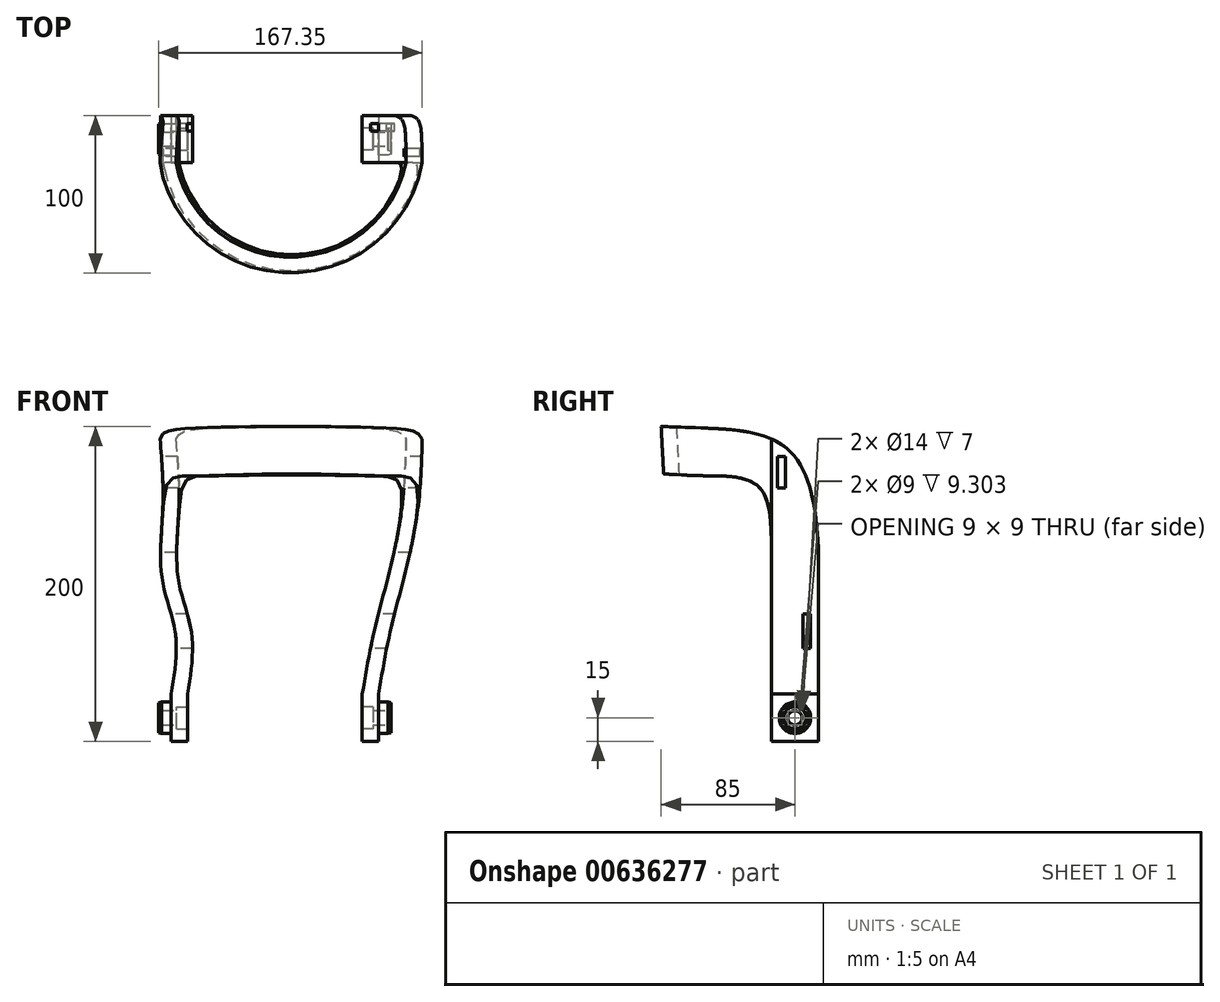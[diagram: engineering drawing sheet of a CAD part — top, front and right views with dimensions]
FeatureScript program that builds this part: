
annotation { "Feature Type Name" : "Feature", "Feature Type Description" : "" }
export const myFeature = defineFeature(function(context is Context, id is Id, definition is map)
    precondition{}
    {
        {
            var Q0;
            Q0=qCreatedBy(makeId("Top.planeOp"),FACE);
            var sketch = newSketch(context, id + "F0", { "sketchPlane" : qUnion([Q0])});
            skLineSegment(sketch, "E0", {"start": v(-55.5, 15) * mm, "end": v(-55.5, -15) * mm});
            skLineSegment(sketch, "E1", {"start": v(55.5, 15) * mm, "end": v(55.5, -15) * mm});
            skPoint(sketch, "E2", {"position": v(-55.5, 0) * mm});
            skPoint(sketch, "E3", {"position": v(55.5, 0) * mm});
            skLineSegment(sketch, "E4", {"start": v(-55.5, 15) * mm, "end": v(-65.81, 15) * mm});
            skLineSegment(sketch, "E5", {"start": v(-65.81, 15) * mm, "end": v(-65.81, -15) * mm});
            skLineSegment(sketch, "E6", {"start": v(55.5, 15) * mm, "end": v(65.81, 15) * mm});
            skLineSegment(sketch, "E7", {"start": v(65.81, 15) * mm, "end": v(65.81, -15) * mm});
            skLineSegment(sketch, "E8", {"start": v(-65.81, -15) * mm, "end": v(-55.5, -15) * mm});
            skLineSegment(sketch, "E9", {"start": v(55.5, -15) * mm, "end": v(65.81, -15) * mm});
            skSolve(sketch);
        }
        {
            var Q0;
            Q0=qCreatedBy(makeId("Top.planeOp"),FACE);
            cPlane(context, id + "F1", {"entities" : qUnion([Q0]), "cplaneType" : CPlaneType.OFFSET, "offset" : 30 * mm, "width" : 150 * mm, "height" : 150 * mm});
        }
        {
            var Q0;
            Q0=qCreatedBy(id+"F1.planeOp",FACE);
            var sketch = newSketch(context, id + "F2", { "sketchPlane" : qUnion([Q0])});
            skArc(sketch, "E10", {"start": v(-55.5, -15) * mm, "mid": v(0, -57.5) * mm, "end": v(55.5, -15) * mm});
            skArc(sketch, "E11", {"start": v(-65.81, -15) * mm, "mid": v(0, -67.5) * mm, "end": v(65.81, -15) * mm});
            skLineSegment(sketch, "E12", {"start": v(-55.5, 15) * mm, "end": v(-55.5, -15) * mm});
            skLineSegment(sketch, "E13", {"start": v(55.5, 15) * mm, "end": v(55.5, -15) * mm});
            skPoint(sketch, "E14", {"position": v(-55.5, 0) * mm});
            skPoint(sketch, "E15", {"position": v(55.5, 0) * mm});
            skLineSegment(sketch, "E16", {"start": v(-55.5, 15) * mm, "end": v(-65.81, 15) * mm});
            skLineSegment(sketch, "E17", {"start": v(-65.81, 15) * mm, "end": v(-65.81, -15) * mm});
            skLineSegment(sketch, "E18", {"start": v(55.5, 15) * mm, "end": v(65.81, 15) * mm});
            skLineSegment(sketch, "E19", {"start": v(65.81, 15) * mm, "end": v(65.81, -15) * mm});
            skSolve(sketch);
        }
        {
            var Q0;
            Q0=qCreatedBy(makeId("Top.planeOp"),FACE);
            cPlane(context, id + "F3", {"entities" : qUnion([Q0]), "cplaneType" : CPlaneType.OFFSET, "offset" : 70 * mm, "width" : 150 * mm, "height" : 150 * mm});
        }
        {
            var Q0;
            Q0=qCreatedBy(id+"F3.planeOp",FACE);
            var sketch = newSketch(context, id + "F4", { "sketchPlane" : qUnion([Q0])});
            skPoint(sketch, "E20", {"position": v(5, 0) * mm});
            skPoint(sketch, "E21.center.orphan", {"position": v(0, 0) * mm});
            skArc(sketch, "E22", {"start": v(-53.1, -15) * mm, "mid": v(5, -60) * mm, "end": v(63.1, -15) * mm});
            skArc(sketch, "E23", {"start": v(-63.37, -15) * mm, "mid": v(5, -70) * mm, "end": v(73.37, -15) * mm});
            skLineSegment(sketch, "E24", {"start": v(-53.1, 15) * mm, "end": v(-53.1, -15) * mm});
            skLineSegment(sketch, "E25", {"start": v(63.1, 15) * mm, "end": v(63.1, -15) * mm});
            skPoint(sketch, "E26", {"position": v(-53.1, 0) * mm});
            skLineSegment(sketch, "E27", {"start": v(-53.1, 15) * mm, "end": v(-63.37, 15) * mm});
            skLineSegment(sketch, "E28", {"start": v(-63.37, 15) * mm, "end": v(-63.37, -15) * mm});
            skLineSegment(sketch, "E29", {"start": v(63.1, 15) * mm, "end": v(73.37, 15) * mm});
            skLineSegment(sketch, "E30", {"start": v(73.37, 15) * mm, "end": v(73.37, -15) * mm});
            skSolve(sketch);
        }
        {
            var Q0;
            Q0=qCreatedBy(makeId("Top.planeOp"),FACE);
            cPlane(context, id + "F5", {"entities" : qUnion([Q0]), "cplaneType" : CPlaneType.OFFSET, "offset" : 100 * mm, "width" : 150 * mm, "height" : 150 * mm});
        }
        {
            var Q0;
            Q0=qCreatedBy(id+"F5.planeOp",FACE);
            var sketch = newSketch(context, id + "F6", { "sketchPlane" : qUnion([Q0])});
            skPoint(sketch, "E31", {"position": v(5, 0) * mm});
            skArc(sketch, "E32", {"start": v(-60.81, -15) * mm, "mid": v(5, -67.5) * mm, "end": v(70.81, -15) * mm});
            skArc(sketch, "E33", {"start": v(-71.03, -15) * mm, "mid": v(5, -77.5) * mm, "end": v(81.03, -15) * mm});
            skLineSegment(sketch, "E34", {"start": v(-60.81, 15) * mm, "end": v(-60.81, -15) * mm});
            skLineSegment(sketch, "E35", {"start": v(70.81, 15) * mm, "end": v(70.81, -15) * mm});
            skLineSegment(sketch, "E36", {"start": v(-60.81, 15) * mm, "end": v(-71.03, 15) * mm});
            skLineSegment(sketch, "E37", {"start": v(-71.03, 15) * mm, "end": v(-71.03, -15) * mm});
            skLineSegment(sketch, "E38", {"start": v(70.81, 15) * mm, "end": v(81.03, 15) * mm});
            skLineSegment(sketch, "E39", {"start": v(81.03, 15) * mm, "end": v(81.03, -15) * mm});
            skSolve(sketch);
        }
        {
            var Q0;
            Q0=qCreatedBy(makeId("Top.planeOp"),FACE);
            cPlane(context, id + "F7", {"entities" : qUnion([Q0]), "cplaneType" : CPlaneType.OFFSET, "offset" : 150 * mm, "width" : 150 * mm, "height" : 150 * mm});
        }
        {
            var Q0;
            Q0=qCreatedBy(id+"F7.planeOp",FACE);
            var sketch = newSketch(context, id + "F8", { "sketchPlane" : qUnion([Q0])});
            skPoint(sketch, "E40", {"position": v(10, 0) * mm});
            skArc(sketch, "E41", {"start": v(-60.93, -15) * mm, "mid": v(10, -72.5) * mm, "end": v(80.93, -15) * mm});
            skArc(sketch, "E42", {"start": v(-71.12, -15) * mm, "mid": v(10, -82.5) * mm, "end": v(91.12, -15) * mm});
            skLineSegment(sketch, "E43", {"start": v(-60.93, 15) * mm, "end": v(-60.93, -15) * mm});
            skLineSegment(sketch, "E44", {"start": v(80.93, -15) * mm, "end": v(80.93, 15) * mm});
            skPoint(sketch, "E45", {"position": v(-60.93, 0) * mm});
            skPoint(sketch, "E46", {"position": v(80.93, 0) * mm});
            skLineSegment(sketch, "E47", {"start": v(-60.93, 15) * mm, "end": v(-71.12, 15) * mm});
            skLineSegment(sketch, "E48", {"start": v(-71.12, 15) * mm, "end": v(-71.12, -15) * mm});
            skLineSegment(sketch, "E49", {"start": v(80.93, 15) * mm, "end": v(91.12, 15) * mm});
            skLineSegment(sketch, "E50", {"start": v(91.12, 15) * mm, "end": v(91.12, -15) * mm});
            skSolve(sketch);
        }
        {
            var Q0;
            Q0=qCreatedBy(makeId("Top.planeOp"),FACE);
            cPlane(context, id + "F9", {"entities" : qUnion([Q0]), "cplaneType" : CPlaneType.OFFSET, "offset" : 200 * mm, "width" : 150 * mm, "height" : 150 * mm});
        }
        {
            var Q0;
            Q0=qCreatedBy(id+"F9.planeOp",FACE);
            var sketch = newSketch(context, id + "F10", { "sketchPlane" : qUnion([Q0])});
            skPoint(sketch, "E51", {"position": v(10, 0) * mm});
            skArc(sketch, "E52", {"start": v(-63.48, -15) * mm, "mid": v(10, -75) * mm, "end": v(83.48, -15) * mm});
            skArc(sketch, "E53", {"start": v(-73.67, -15) * mm, "mid": v(10, -85) * mm, "end": v(93.67, -15) * mm});
            skLineSegment(sketch, "E54", {"start": v(-63.48, 15) * mm, "end": v(-63.48, -15) * mm});
            skLineSegment(sketch, "E55", {"start": v(83.48, 15) * mm, "end": v(83.48, -15) * mm});
            skLineSegment(sketch, "E56", {"start": v(-63.48, 15) * mm, "end": v(-73.67, 15) * mm});
            skLineSegment(sketch, "E57", {"start": v(-73.67, 15) * mm, "end": v(-73.67, -15) * mm});
            skLineSegment(sketch, "E58", {"start": v(83.48, 15) * mm, "end": v(93.67, 15) * mm});
            skLineSegment(sketch, "E59", {"start": v(93.67, 15) * mm, "end": v(93.67, -15) * mm});
            skSolve(sketch);
        }
        {
            var Q0;
            Q0=qSketchRegion(id+"F2",true);
            var Q1;
            Q1=qSketchRegion(id+"F4",true);
            var Q2;
            Q2=qSketchRegion(id+"F6",true);
            var Q3;
            Q3=qSketchRegion(id+"F8",true);
            var Q4;
            Q4=qSketchRegion(id+"F10",true);
            loft(context, id + "F11", {"sheetProfilesArray" : [{ "sheetProfileEntities" : qUnion([Q0]) }, { "sheetProfileEntities" : qUnion([Q1]) }, { "sheetProfileEntities" : qUnion([Q2]) }, { "sheetProfileEntities" : qUnion([Q3]) }, { "sheetProfileEntities" : qUnion([Q4]) }]});
        }
        {
            var Q0;
            Q0=qCreatedBy(makeId("Right.planeOp"),FACE);
            cPlane(context, id + "F12", {"entities" : qUnion([Q0]), "cplaneType" : CPlaneType.OFFSET, "offset" : 77 * mm, "oppositeDirection" : true, "width" : 150 * mm, "height" : 150 * mm});
        }
        {
            var Q0;
            Q0=qCreatedBy(id+"F12.planeOp",FACE);
            var sketch = newSketch(context, id + "F13", { "sketchPlane" : qUnion([Q0])});
            skPoint(sketch, "E60", {"position": v(-85, 200) * mm});
            skLineSegment(sketch, "E61", {"start": v(-85, 200) * mm, "end": v(-85, 170) * mm});
            skPoint(sketch, "E62", {"position": v(15, 200) * mm});
            skLineSegment(sketch, "E63", {"start": v(15, 200) * mm, "end": v(15, 120) * mm});
            skPoint(sketch, "E64", {"position": v(15, 0) * mm});
            skPoint(sketch, "E65", {"position": v(-15, 0) * mm});
            skPoint(sketch, "E66", {"position": v(-15, 200) * mm});
            skFitSpline(sketch, "E67", {"points": [v(-85, 200) * mm, v(15, 120) * mm], "startDerivative": vector(199.24, -8.69) * mm, "endDerivative": vector(9.95, -251.27) * mm});
            skPoint(sketch, "E68", {"position": v(-56.51, 168.7) * mm});
            skPoint(sketch, "E69", {"position": v(-23.21, 161.98) * mm});
            skPoint(sketch, "E70", {"position": v(-50.86, 198.7) * mm});
            skPoint(sketch, "E71", {"position": v(-4.39, 185.34) * mm});
            skPoint(sketch, "E72", {"position": v(-15, 120) * mm});
            skFitSpline(sketch, "E73", {"points": [v(-15, 120) * mm, v(-23.21, 161.98) * mm, v(-56.51, 168.7) * mm, v(-85, 170) * mm], "startDerivative": vector(0.5, 138.75) * mm, "endDerivative": vector(-88.02, 5.85) * mm});
            skLineSegment(sketch, "E74", {"start": v(-15, 120) * mm, "end": v(-15, 0) * mm});
            skLineSegment(sketch, "E75", {"start": v(15, 0) * mm, "end": v(15, 120) * mm});
            skLineSegment(sketch, "E76", {"start": v(-85, 200) * mm, "end": v(15, 200) * mm});
            skLineSegment(sketch, "E77", {"start": v(-85, 170) * mm, "end": v(-82.46, 0) * mm});
            skLineSegment(sketch, "E78", {"start": v(-82.46, 0) * mm, "end": v(-15, 0) * mm});
            skLineSegment(sketch, "E79", {"start": v(-85, 170) * mm, "end": v(-85, 200) * mm});
            skSolve(sketch);
        }
        {
            var Q0;
            Q0=qSketchRegion(id+"F13",true);
            extrude(context, id + "F14", {"entities" : qUnion([Q0]), "operationType" : NewBodyOperationType.REMOVE, "depth" : 300 * mm, "offsetDistance" : 25 * mm});
        }
        {
            var Q0;
            Q0=qCreatedBy(id+"F12.planeOp",FACE);
            var sketch = newSketch(context, id + "F15", { "sketchPlane" : qUnion([Q0])});
            skPoint(sketch, "E80", {"position": v(7.5, 70) * mm});
            skLineSegment(sketch, "E81.bottom", {"start": v(10, 81) * mm, "end": v(5, 81) * mm});
            skLineSegment(sketch, "E81.top", {"start": v(10, 59) * mm, "end": v(5, 59) * mm});
            skLineSegment(sketch, "E81.left", {"start": v(10, 81) * mm, "end": v(10, 59) * mm});
            skLineSegment(sketch, "E81.right", {"start": v(5, 81) * mm, "end": v(5, 59) * mm});
            skPoint(sketch, "E82", {"position": v(15, 0) * mm});
            skLineSegment(sketch, "E83", {"start": v(15, 0) * mm, "end": v(15, 89.37) * mm});
            skPoint(sketch, "E84", {"position": v(15, 70) * mm});
            skSolve(sketch);
        }
        {
            var Q0;
            Q0=qSketchRegion(id+"F15",true);
            extrude(context, id + "F16", {"entities" : qUnion([Q0]), "operationType" : NewBodyOperationType.REMOVE, "depth" : 192.9 * mm, "offsetDistance" : 25 * mm});
        }
        {
            var Q0;
            Q0=qCreatedBy(id+"F12.planeOp",FACE);
            var sketch = newSketch(context, id + "F17", { "sketchPlane" : qUnion([Q0])});
            skPoint(sketch, "E85", {"position": v(-8.62, 171.05) * mm});
            skLineSegment(sketch, "E86.bottom", {"start": v(-11.12, 161.05) * mm, "end": v(-6.12, 161.05) * mm});
            skLineSegment(sketch, "E86.top", {"start": v(-11.12, 181.05) * mm, "end": v(-6.12, 181.05) * mm});
            skLineSegment(sketch, "E86.left", {"start": v(-11.12, 161.05) * mm, "end": v(-11.12, 181.05) * mm});
            skLineSegment(sketch, "E86.right", {"start": v(-6.12, 161.05) * mm, "end": v(-6.12, 181.05) * mm});
            skSolve(sketch);
        }
        {
            var Q0;
            Q0=qSketchRegion(id+"F17",true);
            extrude(context, id + "F18", {"entities" : qUnion([Q0]), "operationType" : NewBodyOperationType.REMOVE, "depth" : 239 * mm, "offsetDistance" : 25 * mm});
        }
        {
            var Q0;
            Q0=qSketchRegion(id+"F0",true);
            extrude(context, id + "F19", {"entities" : qUnion([Q0]), "operationType" : NewBodyOperationType.ADD, "depth" : 30 * mm, "offsetDistance" : 25 * mm});
        }
        {
            var Q0;
            Q0=makeQuery(id+"F19.opExtrude","SWEPT_FACE",FACE,{"disambiguationData":[OSD([sQuery(id+"F0.wireOp",EDGE,"E7")])]});
            var sketch = newSketch(context, id + "F20", { "sketchPlane" : qUnion([Q0])});
            skPoint(sketch, "E87", {"position": v(-15, 30) * mm});
            skPoint(sketch, "E88", {"position": v(-15, 0) * mm});
            skPoint(sketch, "E89", {"position": v(0, 15) * mm});
            skCircle(sketch, "E90", {"center": v(0, 15) * mm, "radius": 10 * mm});
            skSolve(sketch);
        }
        {
            var Q0;
            Q0=qSketchRegion(id+"F20",true);
            extrude(context, id + "F21", {"entities" : qUnion([Q0]), "operationType" : NewBodyOperationType.ADD, "depth" : 6 * mm, "offsetDistance" : 25 * mm});
        }
        {
            var Q0;
            Q0=makeQuery(id+"F21.opExtrude","CAP_FACE",FACE,{"disambiguationData":[OSD([sQuery(id+"F20.wireOp",EDGE,"E90")])],"isStart":false});
            cPlane(context, id + "F22", {"entities" : qUnion([Q0]), "cplaneType" : CPlaneType.OFFSET, "offset" : 0 * mm, "width" : 150 * mm, "height" : 150 * mm});
        }
        {
            var Q0;
            Q0=makeQuery(id+"F19.opExtrude","SWEPT_FACE",FACE,{"disambiguationData":[OSD([sQuery(id+"F0.wireOp",EDGE,"E1")])]});
            cPlane(context, id + "F23", {"entities" : qUnion([Q0]), "cplaneType" : CPlaneType.OFFSET, "offset" : 0 * mm, "width" : 150 * mm, "height" : 150 * mm});
        }
        {
            var Q0;
            Q0=qCreatedBy(id+"F23.planeOp",FACE);
            var sketch = newSketch(context, id + "F24", { "sketchPlane" : qUnion([Q0])});
            skPoint(sketch, "E91", {"position": v(0, 0) * mm});
            skPoint(sketch, "E92", {"position": v(0, 15) * mm});
            skCircle(sketch, "E93", {"center": v(0, 15) * mm, "radius": 7 * mm});
            skSolve(sketch);
        }
        {
            var Q0;
            Q0=qSketchRegion(id+"F24",true);
            extrude(context, id + "F25", {"entities" : qUnion([Q0]), "operationType" : NewBodyOperationType.REMOVE, "oppositeDirection" : true, "depth" : 7 * mm, "offsetDistance" : 25 * mm});
        }
        {
            var Q0;
            Q0=makeQuery(id+"F19.opExtrude","SWEPT_FACE",FACE,{"disambiguationData":[OSD([sQuery(id+"F0.wireOp",EDGE,"E5")])]});
            cPlane(context, id + "F26", {"entities" : qUnion([Q0]), "cplaneType" : CPlaneType.OFFSET, "offset" : 0 * mm, "width" : 150 * mm, "height" : 150 * mm});
        }
        {
            var Q0;
            Q0=qCreatedBy(id+"F26.planeOp",FACE);
            var sketch = newSketch(context, id + "F27", { "sketchPlane" : qUnion([Q0])});
            skPoint(sketch, "E94", {"position": v(0, 15) * mm});
            skCircle(sketch, "E95", {"center": v(0, 15) * mm, "radius": 10 * mm});
            skSolve(sketch);
        }
        {
            var Q0;
            Q0=qSketchRegion(id+"F27",true);
            extrude(context, id + "F28", {"entities" : qUnion([Q0]), "operationType" : NewBodyOperationType.ADD, "depth" : 6 * mm, "offsetDistance" : 25 * mm});
        }
        {
            var Q0;
            Q0=makeQuery(id+"F28.opExtrude","CAP_FACE",FACE,{"disambiguationData":[OSD([sQuery(id+"F27.wireOp",EDGE,"E95")])],"isStart":false});
            cPlane(context, id + "F29", {"entities" : qUnion([Q0]), "cplaneType" : CPlaneType.OFFSET, "offset" : 0 * mm, "width" : 150 * mm, "height" : 150 * mm});
        }
        {
            var Q0;
            Q0=makeQuery(id+"F19.opExtrude","SWEPT_FACE",FACE,{"disambiguationData":[OSD([sQuery(id+"F0.wireOp",EDGE,"E0")])]});
            cPlane(context, id + "F30", {"entities" : qUnion([Q0]), "cplaneType" : CPlaneType.OFFSET, "offset" : 0 * mm, "width" : 150 * mm, "height" : 150 * mm});
        }
        {
            var Q0;
            Q0=qCreatedBy(id+"F30.planeOp",FACE);
            var sketch = newSketch(context, id + "F31", { "sketchPlane" : qUnion([Q0])});
            skPoint(sketch, "E96", {"position": v(0, 0) * mm});
            skPoint(sketch, "E97", {"position": v(0, 15) * mm});
            skCircle(sketch, "E98", {"center": v(0, 15) * mm, "radius": 7 * mm});
            skSolve(sketch);
        }
        {
            var Q0;
            Q0=qSketchRegion(id+"F31",true);
            extrude(context, id + "F32", {"entities" : qUnion([Q0]), "operationType" : NewBodyOperationType.REMOVE, "oppositeDirection" : true, "depth" : 7 * mm, "offsetDistance" : 25 * mm});
        }
        {
            var Q0;
            Q0=makeQuery(id+"F19.opExtrude","CAP_FACE",FACE,{"disambiguationData":[OSD([sQuery(id+"F0.wireOp",EDGE,"E1"),sQuery(id+"F0.wireOp",EDGE,"E6"),sQuery(id+"F0.wireOp",EDGE,"E7"),sQuery(id+"F0.wireOp",EDGE,"E9")])],"isStart":true});
            cPlane(context, id + "F33", {"entities" : qUnion([Q0]), "cplaneType" : CPlaneType.OFFSET, "offset" : 15 * mm, "oppositeDirection" : true, "width" : 150 * mm, "height" : 150 * mm});
        }
        {
            var Q0;
            Q0=qCreatedBy(id+"F33.planeOp",FACE);
            var sketch = newSketch(context, id + "F34", { "sketchPlane" : qUnion([Q0])});
            skPoint(sketch, "E99", {"position": v(60.66, -15) * mm});
            skLineSegment(sketch, "E100", {"start": v(60.66, -15) * mm, "end": v(61.72, -15) * mm, "construction": true});
            skPoint(sketch, "E101", {"position": v(71.81, 4.05) * mm});
            skPoint(sketch, "E102", {"position": v(71.81, -12) * mm});
            skPoint(sketch, "E103", {"position": v(71.81, -15) * mm});
            skPoint(sketch, "E104", {"position": v(41.37, 7.31) * mm});
            skPoint(sketch, "E105", {"position": v(71.81, -13.5) * mm});
            skPoint(sketch, "E106", {"position": v(73.81, -13.5) * mm});
            skPoint(sketch, "E107", {"position": v(73.81, -12.5) * mm});
            skPoint(sketch, "E108", {"position": v(73.81, -14.5) * mm});
            skLineSegment(sketch, "E109", {"start": v(71.81, -12) * mm, "end": v(71.81, -15) * mm});
            skPoint(sketch, "E110", {"position": v(71.81, 0) * mm});
            skPoint(sketch, "E111", {"position": v(71.81, -10) * mm});
            skPoint(sketch, "E112", {"position": v(65.81, -10) * mm});
            skPoint(sketch, "E113", {"position": v(65.81, -7) * mm});
            skPoint(sketch, "E114", {"position": v(65.81, -8.5) * mm});
            skPoint(sketch, "E115", {"position": v(67.81, -8.5) * mm});
            skPoint(sketch, "E116", {"position": v(67.81, -7.5) * mm});
            skPoint(sketch, "E117", {"position": v(67.81, -9.5) * mm});
            skPoint(sketch, "E118", {"position": v(65.81, 0) * mm});
            skLineSegment(sketch, "E119.trimOffspring", {"start": v(71.81, -10) * mm, "end": v(71.81, -16.41) * mm, "construction": true});
            skPoint(sketch, "E120", {"position": v(71.81, -7) * mm});
            skPoint(sketch, "E121", {"position": v(71.81, -8.5) * mm});
            skPoint(sketch, "E122", {"position": v(73.81, -8.5) * mm});
            skPoint(sketch, "E123", {"position": v(73.81, -7.5) * mm});
            skPoint(sketch, "E124", {"position": v(73.81, -9.5) * mm});
            skLineSegment(sketch, "E125", {"start": v(73.81, -7.5) * mm, "end": v(71.81, -7) * mm});
            skLineSegment(sketch, "E126", {"start": v(73.81, -9.5) * mm, "end": v(73.81, -7.5) * mm});
            skLineSegment(sketch, "E127", {"start": v(73.81, -9.5) * mm, "end": v(71.81, -10) * mm});
            skLineSegment(sketch, "E128", {"start": v(71.81, -7) * mm, "end": v(71.81, -10) * mm});
            skLineSegment(sketch, "E129", {"start": v(71.81, 0) * mm, "end": v(73.81, 0) * mm});
            skLineSegment(sketch, "E130", {"start": v(73.81, -8.5) * mm, "end": v(73.81, -9.5) * mm});
            skSolve(sketch);
        }
        {
            var Q0;
            Q0=qSketchRegion(id+"F34",true);
            var Q1;
            Q1=sQuery(id+"F34.wireOp",EDGE,"E129");
            revolve(context, id + "F35", {"operationType" : NewBodyOperationType.ADD, "entities" : qUnion([Q0]), "axis" : qUnion([Q1]), "revolveType" : RevolveType.FULL});
        }
        {
            var Q0;
            Q0=qCreatedBy(id+"F22.planeOp",FACE);
            var sketch = newSketch(context, id + "F36", { "sketchPlane" : qUnion([Q0])});
            skPoint(sketch, "E131", {"position": v(0, 15) * mm});
            skPoint(sketch, "E132", {"position": v(0, 0) * mm});
            skCircle(sketch, "E133", {"center": v(0, 15) * mm, "radius": 4.5 * mm});
            skSolve(sketch);
        }
        {
            var Q0;
            Q0=qSketchRegion(id+"F36",true);
            extrude(context, id + "F37", {"entities" : qUnion([Q0]), "operationType" : NewBodyOperationType.REMOVE, "oppositeDirection" : true, "depth" : 25 * mm, "offsetDistance" : 25 * mm});
        }
        {
            var Q0;
            Q0=makeQuery(id+"F19.opExtrude","CAP_FACE",FACE,{"disambiguationData":[OSD([sQuery(id+"F0.wireOp",EDGE,"E0"),sQuery(id+"F0.wireOp",EDGE,"E4"),sQuery(id+"F0.wireOp",EDGE,"E5"),sQuery(id+"F0.wireOp",EDGE,"E8")])],"isStart":true});
            cPlane(context, id + "F38", {"entities" : qUnion([Q0]), "cplaneType" : CPlaneType.OFFSET, "offset" : 15 * mm, "oppositeDirection" : true, "width" : 150 * mm, "height" : 150 * mm});
        }
        {
            var Q0;
            Q0=qCreatedBy(id+"F38.planeOp",FACE);
            var sketch = newSketch(context, id + "F39", { "sketchPlane" : qUnion([Q0])});
            skPoint(sketch, "E134", {"position": v(-60.91, -32.93) * mm});
            skPoint(sketch, "E135", {"position": v(-65.81, -10) * mm});
            skPoint(sketch, "E136", {"position": v(-57.6, -34.18) * mm});
            skPoint(sketch, "E137", {"position": v(-65.81, -15) * mm});
            skPoint(sketch, "E138", {"position": v(-71.81, -10) * mm});
            skPoint(sketch, "E139", {"position": v(-71.81, -7) * mm});
            skPoint(sketch, "E140", {"position": v(-71.81, -8.5) * mm});
            skPoint(sketch, "E141", {"position": v(-73.81, -8.5) * mm});
            skPoint(sketch, "E142", {"position": v(-73.81, -9.5) * mm});
            skPoint(sketch, "E143", {"position": v(-73.81, -7.5) * mm});
            skLineSegment(sketch, "E144", {"start": v(-73.81, -9.5) * mm, "end": v(-71.81, -10) * mm});
            skLineSegment(sketch, "E145", {"start": v(-73.81, -7.5) * mm, "end": v(-73.81, -9.5) * mm});
            skLineSegment(sketch, "E146", {"start": v(-73.81, -7.5) * mm, "end": v(-71.81, -7) * mm});
            skLineSegment(sketch, "E147", {"start": v(-71.81, -10) * mm, "end": v(-71.81, -7) * mm});
            skLineSegment(sketch, "E148", {"start": v(-73.81, -8.5) * mm, "end": v(-73.81, -7.5) * mm});
            skSolve(sketch);
        }
        {
            var Q0;
            Q0=qCreatedBy(id+"F38.planeOp",FACE);
            var sketch = newSketch(context, id + "F40", { "sketchPlane" : qUnion([Q0])});
            skPoint(sketch, "E149", {"position": v(-71.81, -10) * mm});
            skPoint(sketch, "E150", {"position": v(-71.81, 0) * mm});
            skLineSegment(sketch, "E151", {"start": v(-71.81, 0) * mm, "end": v(-73.81, 0) * mm});
            skSolve(sketch);
        }
        {
            var Q0;
            Q0=qSketchRegion(id+"F39",true);
            var Q1;
            Q1=sQuery(id+"F40.wireOp",EDGE,"E151");
            revolve(context, id + "F41", {"operationType" : NewBodyOperationType.ADD, "entities" : qUnion([Q0]), "axis" : qUnion([Q1]), "revolveType" : RevolveType.FULL});
        }
        {
            var Q0;
            Q0=qCreatedBy(id+"F30.planeOp",FACE);
            var sketch = newSketch(context, id + "F42", { "sketchPlane" : qUnion([Q0])});
            skPoint(sketch, "E152", {"position": v(0, 0) * mm});
            skPoint(sketch, "E153", {"position": v(0, 15) * mm});
            skCircle(sketch, "E154", {"center": v(0, 15) * mm, "radius": 4.5 * mm});
            skSolve(sketch);
        }
        {
            var Q0;
            Q0=qSketchRegion(id+"F42",true);
            extrude(context, id + "F43", {"entities" : qUnion([Q0]), "operationType" : NewBodyOperationType.REMOVE, "oppositeDirection" : true, "depth" : 25 * mm, "offsetDistance" : 25 * mm});
        }
    });
